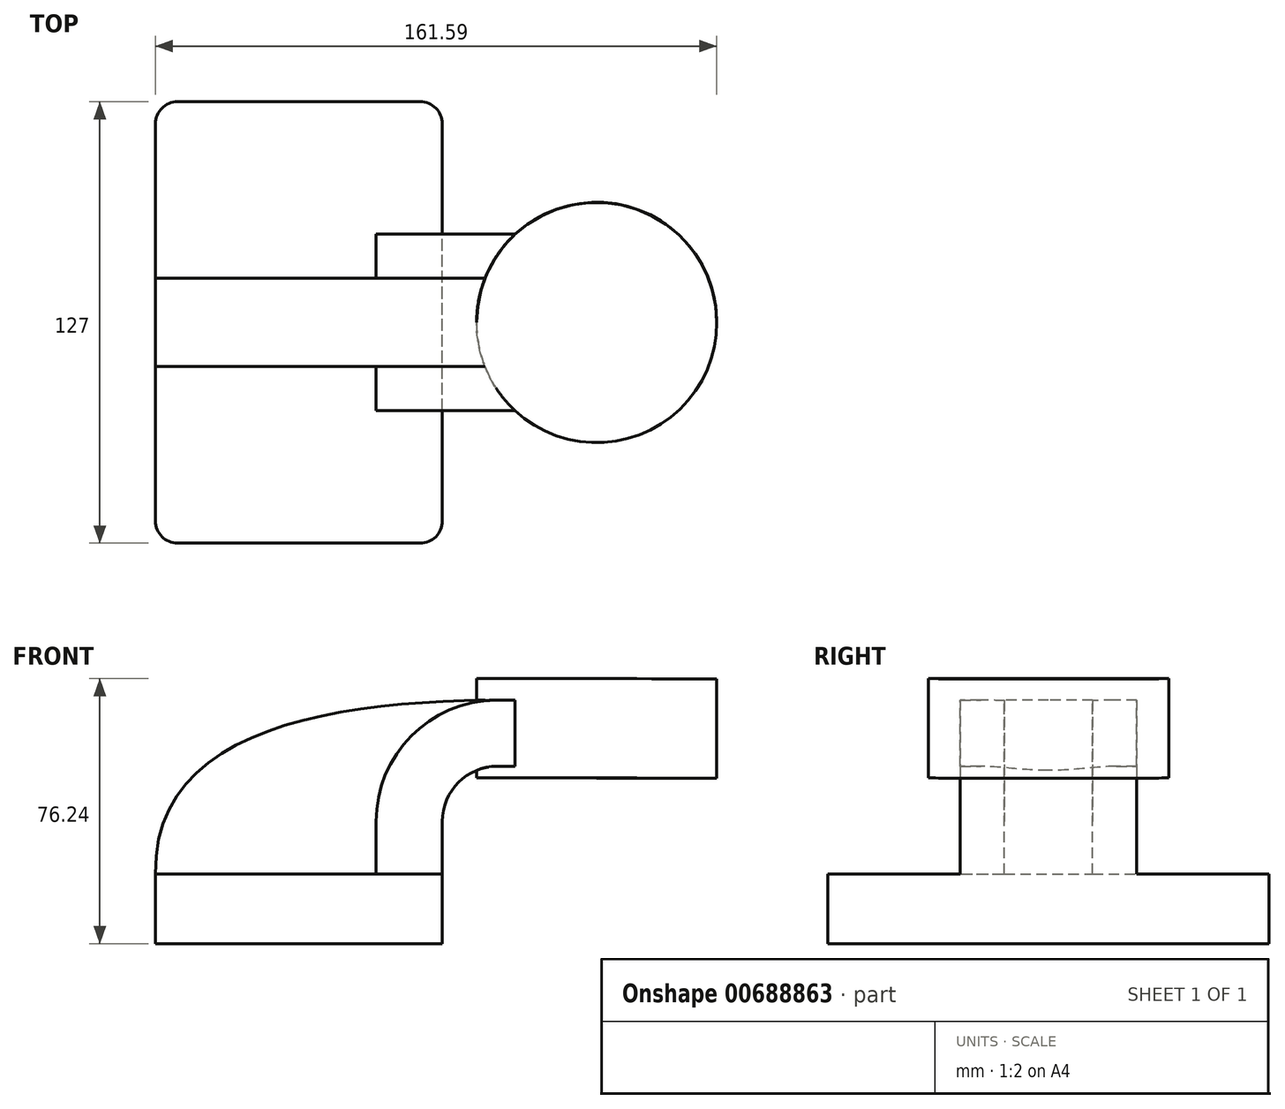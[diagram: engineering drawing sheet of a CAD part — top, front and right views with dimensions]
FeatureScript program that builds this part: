
annotation { "Feature Type Name" : "Feature", "Feature Type Description" : "" }
export const myFeature = defineFeature(function(context is Context, id is Id, definition is map)
    precondition{}
    {
        {
            var Q0;
            Q0=qCreatedBy(makeId("Front.planeOp"),FACE);
            var sketch = newSketch(context, id + "F0", { "sketchPlane" : qUnion([Q0])});
            skLineSegment(sketch, "E0.bottom", {"start": v(41.28, -10) * mm, "end": v(-41.28, -10) * mm});
            skLineSegment(sketch, "E0.top", {"start": v(41.28, 10) * mm, "end": v(-41.28, 10) * mm});
            skLineSegment(sketch, "E0.left", {"start": v(41.28, -10) * mm, "end": v(41.28, 10) * mm});
            skLineSegment(sketch, "E0.right", {"start": v(-41.28, -10) * mm, "end": v(-41.28, 10) * mm});
            skPoint(sketch, "E0.middle", {"position": v(0, 0) * mm});
            skLineSegment(sketch, "E1.bottom", {"start": v(69.5, 66.2) * mm, "end": v(120.3, 66.2) * mm});
            skLineSegment(sketch, "E1.top", {"start": v(69.5, 37.62) * mm, "end": v(120.3, 37.62) * mm});
            skLineSegment(sketch, "E1.left", {"start": v(69.5, 66.2) * mm, "end": v(69.5, 37.62) * mm});
            skLineSegment(sketch, "E1.right", {"start": v(120.3, 66.2) * mm, "end": v(120.3, 37.62) * mm});
            skLineSegment(sketch, "E2", {"start": v(41.28, 10) * mm, "end": v(41.28, 25.14) * mm});
            skArc(sketch, "E3", {"start": v(41.27, 25.14) * mm, "mid": v(45.92, 36.36) * mm, "end": v(57.15, 41.01) * mm});
            skLineSegment(sketch, "E4", {"start": v(57.15, 41.01) * mm, "end": v(85.72, 41.01) * mm});
            skLineSegment(sketch, "E5.0", {"start": v(57.15, 60.06) * mm, "end": v(85.72, 60.06) * mm});
            skArc(sketch, "E5.1", {"start": v(22.23, 25.14) * mm, "mid": v(32.45, 49.83) * mm, "end": v(57.15, 60.06) * mm});
            skLineSegment(sketch, "E5.2", {"start": v(22.23, 10) * mm, "end": v(22.23, 25.14) * mm});
            skLineSegment(sketch, "E6", {"start": v(85.7, 37.62) * mm, "end": v(85.72, 66.2) * mm});
            skFitSpline(sketch, "E7", {"points": [v(-41.28, 10) * mm, v(57.15, 60.06) * mm], "startDerivative": vector(-2.64, 126.2) * mm, "endDerivative": vector(140.61, 0.66) * mm});
            skSolve(sketch);
        }
        {
            var Q0;
            Q0=makeQuery(id+"F0.imprint","IMPRINT",FACE,{"disambiguationData":[TD([[makeQuery(id+"F0.imprint","IMPRINT",EDGE,{"derivedFrom":sQuery(id+"F0.wireOp",EDGE,"E0.bottom")}),-1.0]])]});
            extrude(context, id + "F1", {"entities" : qUnion([Q0]), "endBound" : BoundingType.SYMMETRIC, "depth" : 127 * mm, "offsetDistance" : 25.4 * mm});
        }
        {
            var Q0;
            {var subQ1=sQuery(id+"F0.wireOp",EDGE,"E2");Q0=makeQuery(id+"F0.imprint","IMPRINT",FACE,{"disambiguationData":[TD([[makeQuery(id+"F0.imprint","IMPRINT",EDGE,{"derivedFrom":subQ1}),1.0]])]});}
            var Q1;
            {var subQ0=sQuery(id+"F0.wireOp",EDGE,"E5.0");var subQ1=sQuery(id+"F0.wireOp",EDGE,"E1.left");var subQ2=makeQuery(id+"F0.imprint","INTERSECT",VERTEX,{"derivedFrom":[subQ1,subQ0]});Q1=makeQuery(id+"F0.imprint","IMPRINT",FACE,{"disambiguationData":[TD([[makeQuery(id+"F0.imprint","IMPRINT",EDGE,{"disambiguationData":[TD([[subQ2,-1.0]])],"derivedFrom":subQ1}),1.0]])]});}
            extrude(context, id + "F2", {"entities" : qUnion([Q0, Q1]), "operationType" : NewBodyOperationType.ADD, "endBound" : BoundingType.SYMMETRIC, "depth" : 50.8 * mm, "offsetDistance" : 25.4 * mm});
        }
        {
            var Q0;
            {var subQ4=sQuery(id+"F0.wireOp",EDGE,"E1.right");Q0=makeQuery(id+"F0.imprint","IMPRINT",FACE,{"disambiguationData":[TD([[makeQuery(id+"F0.imprint","IMPRINT",EDGE,{"derivedFrom":subQ4}),-1.0]])]});}
            var Q1;
            Q1=sQuery(id+"F0.wireOp",EDGE,"E6");
            revolve(context, id + "F3", {"operationType" : NewBodyOperationType.ADD, "entities" : qUnion([Q0]), "axis" : qUnion([Q1]), "revolveType" : RevolveType.FULL});
        }
        {
            var Q0;
            Q0=makeQuery(id+"F1.opExtrude","CAP_EDGE",EDGE,{"disambiguationData":[OSD([sQuery(id+"F0.wireOp",EDGE,"E0.right")])],"isStart":false});
            var Q1;
            Q1=makeQuery(id+"F1.opExtrude","CAP_EDGE",EDGE,{"disambiguationData":[OSD([sQuery(id+"F0.wireOp",EDGE,"E0.left")])],"isStart":false});
            var Q2;
            Q2=makeQuery(id+"F1.opExtrude","CAP_EDGE",EDGE,{"disambiguationData":[OSD([sQuery(id+"F0.wireOp",EDGE,"E0.left")])],"isStart":true});
            var Q3;
            Q3=makeQuery(id+"F1.opExtrude","CAP_EDGE",EDGE,{"disambiguationData":[OSD([sQuery(id+"F0.wireOp",EDGE,"E0.right")])],"isStart":true});
            fillet(context, id + "F4", {"entities" : qUnion([Q0, Q1, Q2, Q3]), "radius" : 6.35 * mm, "tangentPropagation" : true, "allowEdgeOverflow" : false});
        }
        {
            var Q0;
            {var subQ3=sQuery(id+"F0.wireOp",EDGE,"E5.2");Q0=makeQuery(id+"F0.imprint","IMPRINT",FACE,{"disambiguationData":[TD([[makeQuery(id+"F0.imprint","IMPRINT",EDGE,{"derivedFrom":subQ3}),1.0]])]});}
            extrude(context, id + "F5", {"entities" : qUnion([Q0]), "operationType" : NewBodyOperationType.ADD, "endBound" : BoundingType.SYMMETRIC, "depth" : 25.4 * mm, "offsetDistance" : 25.4 * mm});
        }
    });
